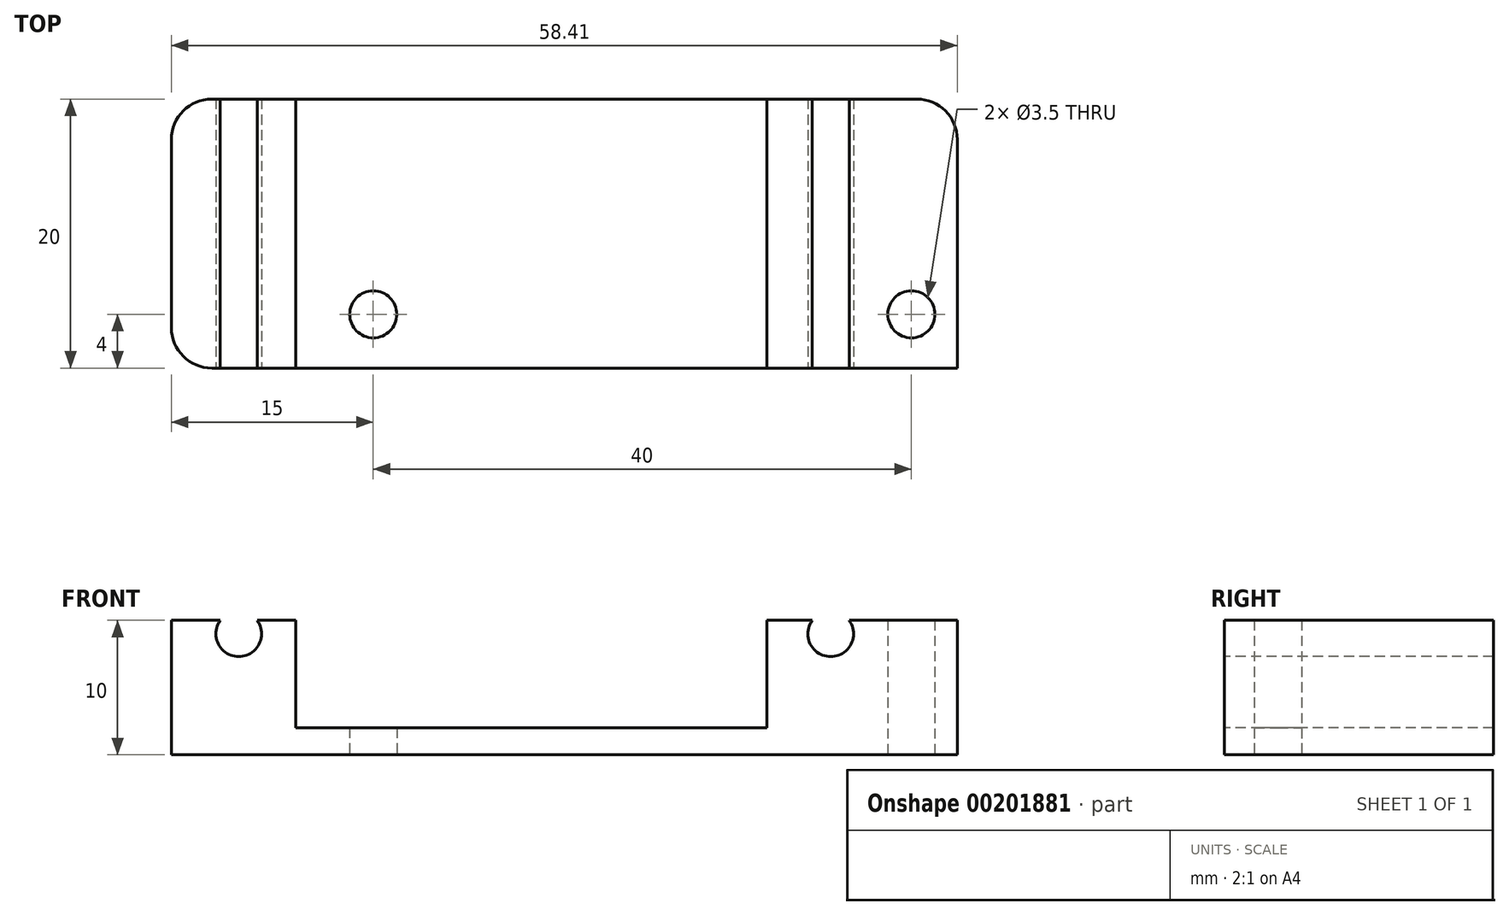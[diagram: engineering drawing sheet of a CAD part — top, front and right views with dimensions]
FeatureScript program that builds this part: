
annotation { "Feature Type Name" : "Feature", "Feature Type Description" : "" }
export const myFeature = defineFeature(function(context is Context, id is Id, definition is map)
    precondition{}
    {
        {
            var Q0;
            Q0=qCreatedBy(makeId("Top.planeOp"),FACE);
            var sketch = newSketch(context, id + "F0", { "sketchPlane" : qUnion([Q0])});
            skLineSegment(sketch, "E0.bottom", {"start": v(50, 10) * mm, "end": v(-50, 10) * mm});
            skLineSegment(sketch, "E0.top", {"start": v(50, -10) * mm, "end": v(-50, -10) * mm});
            skLineSegment(sketch, "E0.left", {"start": v(50, 10) * mm, "end": v(50, -10) * mm});
            skLineSegment(sketch, "E0.right", {"start": v(-50, 10) * mm, "end": v(-50, -10) * mm});
            skPoint(sketch, "E0.middle", {"position": v(0, 0) * mm});
            skSolve(sketch);
        }
        {
            var Q0;
            Q0=makeQuery(id+"F0.imprint","IMPRINT",FACE,{"disambiguationData":[TD([[makeQuery(id+"F0.imprint","IMPRINT",EDGE,{"derivedFrom":sQuery(id+"F0.wireOp",EDGE,"E0.bottom")}),1.0]])]});
            extrude(context, id + "F1", {"entities" : qUnion([Q0]), "depth" : 20 * mm});
        }
        {
            var Q0;
            Q0=makeQuery(id+"F1.opExtrude","SWEPT_FACE",FACE,{"disambiguationData":[OSD([sQuery(id+"F0.wireOp",EDGE,"E0.top")])]});
            var sketch = newSketch(context, id + "F2", { "sketchPlane" : qUnion([Q0])});
            skCircle(sketch, "E1", {"center": v(-45, 19) * mm, "radius": 1.7 * mm});
            skCircle(sketch, "E2", {"center": v(-1, 19) * mm, "radius": 1.7 * mm});
            skSolve(sketch);
        }
        {
            var Q0;
            {var subQ0=sQuery(id+"F2.wireOp",EDGE,"E1");var subQ1=makeQuery(id+"F1.opExtrude","CAP_EDGE",EDGE,{"disambiguationData":[OSD([sQuery(id+"F0.wireOp",EDGE,"E0.top")])],"isStart":false});var subQ2=makeQuery(id+"F2.imprint","INTERSECT",VERTEX,{"disambiguationData":[OD(0.0)],"derivedFrom":[subQ1,subQ0]});Q0=makeQuery(id+"F2.imprint","IMPRINT",FACE,{"disambiguationData":[TD([[makeQuery(id+"F2.imprint","IMPRINT",EDGE,{"disambiguationData":[TD([[subQ2,-1.0]])],"derivedFrom":subQ0}),1.0]])]});}
            var Q1;
            {var subQ0=sQuery(id+"F2.wireOp",EDGE,"E2");var subQ1=makeQuery(id+"F1.opExtrude","CAP_EDGE",EDGE,{"disambiguationData":[OSD([sQuery(id+"F0.wireOp",EDGE,"E0.top")])],"isStart":false});var subQ2=makeQuery(id+"F2.imprint","INTERSECT",VERTEX,{"disambiguationData":[OD(0.0)],"derivedFrom":[subQ1,subQ0]});Q1=makeQuery(id+"F2.imprint","IMPRINT",FACE,{"disambiguationData":[TD([[makeQuery(id+"F2.imprint","IMPRINT",EDGE,{"disambiguationData":[TD([[subQ2,1.0]])],"derivedFrom":subQ0}),1.0]])]});}
            extrude(context, id + "F3", {"entities" : qUnion([Q0, Q1]), "operationType" : NewBodyOperationType.REMOVE, "oppositeDirection" : true, "depth" : 25 * mm});
        }
        {
            var Q0;
            Q0=makeQuery(id+"F1.opExtrude","SWEPT_FACE",FACE,{"disambiguationData":[OSD([sQuery(id+"F0.wireOp",EDGE,"E0.top")])]});
            var sketch = newSketch(context, id + "F4", { "sketchPlane" : qUnion([Q0])});
            skLineSegment(sketch, "E3.bottom", {"start": v(8.4, 20) * mm, "end": v(50, 20) * mm});
            skLineSegment(sketch, "E3.top", {"start": v(8.4, 0) * mm, "end": v(50, 0) * mm});
            skLineSegment(sketch, "E3.left", {"start": v(8.4, 20) * mm, "end": v(8.4, 0) * mm});
            skLineSegment(sketch, "E3.right", {"start": v(50, 20) * mm, "end": v(50, 0) * mm});
            skLineSegment(sketch, "E4.bottom", {"start": v(-50, 10) * mm, "end": v(8.4, 10) * mm});
            skLineSegment(sketch, "E4.top", {"start": v(-50, 0) * mm, "end": v(8.4, 0) * mm});
            skLineSegment(sketch, "E4.left", {"start": v(-50, 10) * mm, "end": v(-50, 0) * mm});
            skLineSegment(sketch, "E4.right", {"start": v(8.4, 10) * mm, "end": v(8.4, 0) * mm});
            skLineSegment(sketch, "E5.bottom", {"start": v(-40.75, 20) * mm, "end": v(-5.75, 20) * mm});
            skLineSegment(sketch, "E5.top", {"start": v(-40.75, 12) * mm, "end": v(-5.75, 12) * mm});
            skLineSegment(sketch, "E5.left", {"start": v(-40.75, 20) * mm, "end": v(-40.75, 12) * mm});
            skLineSegment(sketch, "E5.right", {"start": v(-5.75, 20) * mm, "end": v(-5.75, 12) * mm});
            skSolve(sketch);
        }
        {
            var Q0;
            Q0=makeQuery(id+"F4.imprint","IMPRINT",FACE,{"disambiguationData":[TD([[makeQuery(id+"F4.imprint","IMPRINT",EDGE,{"derivedFrom":sQuery(id+"F4.wireOp",EDGE,"E3.bottom")}),1.0]])]});
            var Q1;
            Q1=makeQuery(id+"F4.imprint","IMPRINT",FACE,{"disambiguationData":[TD([[makeQuery(id+"F4.imprint","IMPRINT",EDGE,{"derivedFrom":sQuery(id+"F4.wireOp",EDGE,"E4.bottom")}),-1.0]])]});
            var Q2;
            Q2=makeQuery(id+"F4.imprint","IMPRINT",FACE,{"disambiguationData":[TD([[makeQuery(id+"F4.imprint","IMPRINT",EDGE,{"derivedFrom":sQuery(id+"F4.wireOp",EDGE,"E5.bottom")}),1.0]])]});
            extrude(context, id + "F5", {"entities" : qUnion([Q0, Q1, Q2]), "operationType" : NewBodyOperationType.REMOVE, "oppositeDirection" : true, "depth" : 25 * mm});
        }
        {
            var Q0;
            Q0=makeQuery(id+"F5.boolean.opBoolean","COPY",FACE,{"derivedFrom":makeQuery(id+"F5.opExtrude","SWEPT_FACE",FACE,{"disambiguationData":[OSD([sQuery(id+"F4.wireOp",EDGE,"E4.bottom")])]})});
            var sketch = newSketch(context, id + "F6", { "sketchPlane" : qUnion([Q0])});
            skCircle(sketch, "E6", {"center": v(-35, 6) * mm, "radius": 1.75 * mm});
            skCircle(sketch, "E7", {"center": v(5, 6) * mm, "radius": 1.75 * mm});
            skSolve(sketch);
        }
        {
            var Q0;
            Q0=makeQuery(id+"F6.imprint","IMPRINT",FACE,{"disambiguationData":[TD([[makeQuery(id+"F6.imprint","IMPRINT",EDGE,{"derivedFrom":sQuery(id+"F6.wireOp",EDGE,"E6")}),1.0]])]});
            var Q1;
            Q1=makeQuery(id+"F6.imprint","IMPRINT",FACE,{"disambiguationData":[TD([[makeQuery(id+"F6.imprint","IMPRINT",EDGE,{"derivedFrom":sQuery(id+"F6.wireOp",EDGE,"E7")}),1.0]])]});
            extrude(context, id + "F7", {"entities" : qUnion([Q0, Q1]), "operationType" : NewBodyOperationType.REMOVE, "oppositeDirection" : true, "depth" : 25 * mm});
        }
        {
            var Q0;
            Q0=makeQuery(id+"F1.opExtrude","SWEPT_EDGE",EDGE,{"disambiguationData":[OSD([sQuery(id+"F0.wireOp",EDGE,"E0.top"),sQuery(id+"F0.wireOp",EDGE,"E0.right")])]});
            var Q1;
            Q1=makeQuery(id+"F1.opExtrude","SWEPT_EDGE",EDGE,{"disambiguationData":[OSD([sQuery(id+"F0.wireOp",EDGE,"E0.bottom"),sQuery(id+"F0.wireOp",EDGE,"E0.right")])]});
            var Q2;
            Q2=makeQuery(id+"F5.boolean.opBoolean","INTERSECT",EDGE,{"derivedFrom":[makeQuery(id+"F1.opExtrude","SWEPT_FACE",FACE,{"disambiguationData":[OSD([sQuery(id+"F0.wireOp",EDGE,"E0.bottom")])]}),makeQuery(id+"F5.opExtrude","SWEPT_FACE",FACE,{"disambiguationData":[OSD([sQuery(id+"F4.wireOp",EDGE,"E3.left")])]})]});
            var Q3;
            Q3=makeQuery(id+"F5.boolean.opBoolean","COPY",EDGE,{"derivedFrom":makeQuery(id+"F5.opExtrude","CAP_EDGE",EDGE,{"disambiguationData":[OSD([sQuery(id+"F4.wireOp",EDGE,"E3.left")])],"isStart":true})});
            fillet(context, id + "F8", {"entities" : qUnion([Q0, Q1, Q2, Q3]), "radius" : 3 * mm, "tangentPropagation" : true, "allowEdgeOverflow" : false});
        }
    });
